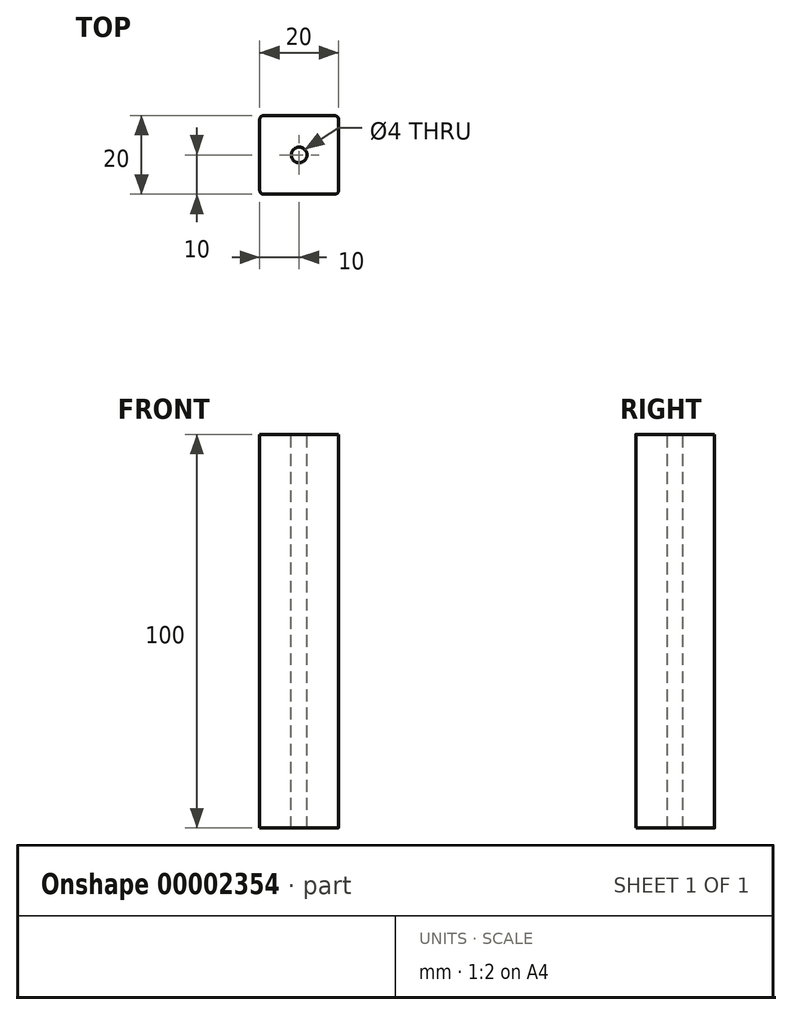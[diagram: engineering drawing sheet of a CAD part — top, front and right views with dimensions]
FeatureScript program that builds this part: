
annotation { "Feature Type Name" : "Feature", "Feature Type Description" : "" }
export const myFeature = defineFeature(function(context is Context, id is Id, definition is map)
    precondition{}
    {
        {
            var Q0;
            Q0=qCreatedBy(makeId("Top.planeOp"),FACE);
            var sketch = newSketch(context, id + "F0", { "sketchPlane" : qUnion([Q0])});
            skLineSegment(sketch, "E0.rect.bottom", {"start": v(10, -10) * mm, "end": v(-10, -10) * mm});
            skLineSegment(sketch, "E0.rect.top", {"start": v(10, 10) * mm, "end": v(-10, 10) * mm});
            skLineSegment(sketch, "E0.rect.left", {"start": v(10, -10) * mm, "end": v(10, 10) * mm});
            skLineSegment(sketch, "E0.rect.right", {"start": v(-10, -10) * mm, "end": v(-10, 10) * mm});
            skPoint(sketch, "E0.rect.middle", {"position": v(0, 0) * mm});
            skSolve(sketch);
        }
        {
            var Q0;
            Q0 = qSketchRegion(id + "F0", true);
            extrude(context, id + "F1", {"entities" : qUnion([Q0]), "depth" : 100 * mm});
        }
        {
            var Q0;
            Q0=makeQuery(id+"F1.opExtrude","CAP_FACE",FACE,{"disambiguationData":[OSD([sQuery(id+"F0.wireOp",EDGE,"E0.rect.bottom"),sQuery(id+"F0.wireOp",EDGE,"E0.rect.top"),sQuery(id+"F0.wireOp",EDGE,"E0.rect.left"),sQuery(id+"F0.wireOp",EDGE,"E0.rect.right")])],"isStart":false});
            var sketch = newSketch(context, id + "F2", { "sketchPlane" : qUnion([Q0])});
            skCircle(sketch, "E1", {"center": v(0, 0) * mm, "radius": 2 * mm});
            skSolve(sketch);
        }
        {
            var Q0;
            Q0 = qSketchRegion(id + "F2", true);
            extrude(context, id + "F3", {"entities" : qUnion([Q0]), "operationType" : NewBodyOperationType.REMOVE, "endBound" : BoundingType.THROUGH_ALL, "oppositeDirection" : true, "depth" : 25 * mm});
        }
        {
            var Q0;
            Q0=makeQuery(id+"F1.opExtrude","SWEPT_EDGE",EDGE,{"disambiguationData":[OSD([sQuery(id+"F0.wireOp",EDGE,"E0.rect.top"),sQuery(id+"F0.wireOp",EDGE,"E0.rect.right")])]});
            var Q1;
            Q1=makeQuery(id+"F1.opExtrude","SWEPT_EDGE",EDGE,{"disambiguationData":[OSD([sQuery(id+"F0.wireOp",EDGE,"E0.rect.bottom"),sQuery(id+"F0.wireOp",EDGE,"E0.rect.right")])]});
            var Q2;
            Q2=makeQuery(id+"F1.opExtrude","SWEPT_EDGE",EDGE,{"disambiguationData":[OSD([sQuery(id+"F0.wireOp",EDGE,"E0.rect.bottom"),sQuery(id+"F0.wireOp",EDGE,"E0.rect.left")])]});
            var Q3;
            Q3=makeQuery(id+"F1.opExtrude","SWEPT_EDGE",EDGE,{"disambiguationData":[OSD([sQuery(id+"F0.wireOp",EDGE,"E0.rect.top"),sQuery(id+"F0.wireOp",EDGE,"E0.rect.left")])]});
            fillet(context, id + "F4", {"entities" : qUnion([Q0, Q1, Q2, Q3]), "radius" : 1 * mm, "tangentPropagation" : true, "allowEdgeOverflow" : false});
        }
    });
